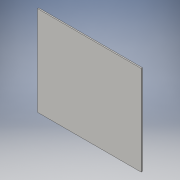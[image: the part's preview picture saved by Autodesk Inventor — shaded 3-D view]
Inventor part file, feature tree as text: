
AUTODESK INVENTOR PART (.ipt)
format: ipt  version: 2016 (Build 200138000, 138)  size: 83,968 bytes
history: native  units: in
note: dims shown in document units (in); Inventor stores cm internally (conversion verified against a paired STEP export)
features: extrude x1, sketch x1
ambient origin geometry x8: Origin, YZ Plane, XZ Plane, XY Plane, X Axis, Y Axis, Z Axis, Center Point
bodies: Solid1 (feature_tree)
feature tree (2):
  extrude  "Extrusion1"  Depth=10.41in
  sketch  "Sketch1"  dims[d0=12.0in d1=10.41in d2=0.15in d3=0.0in]
